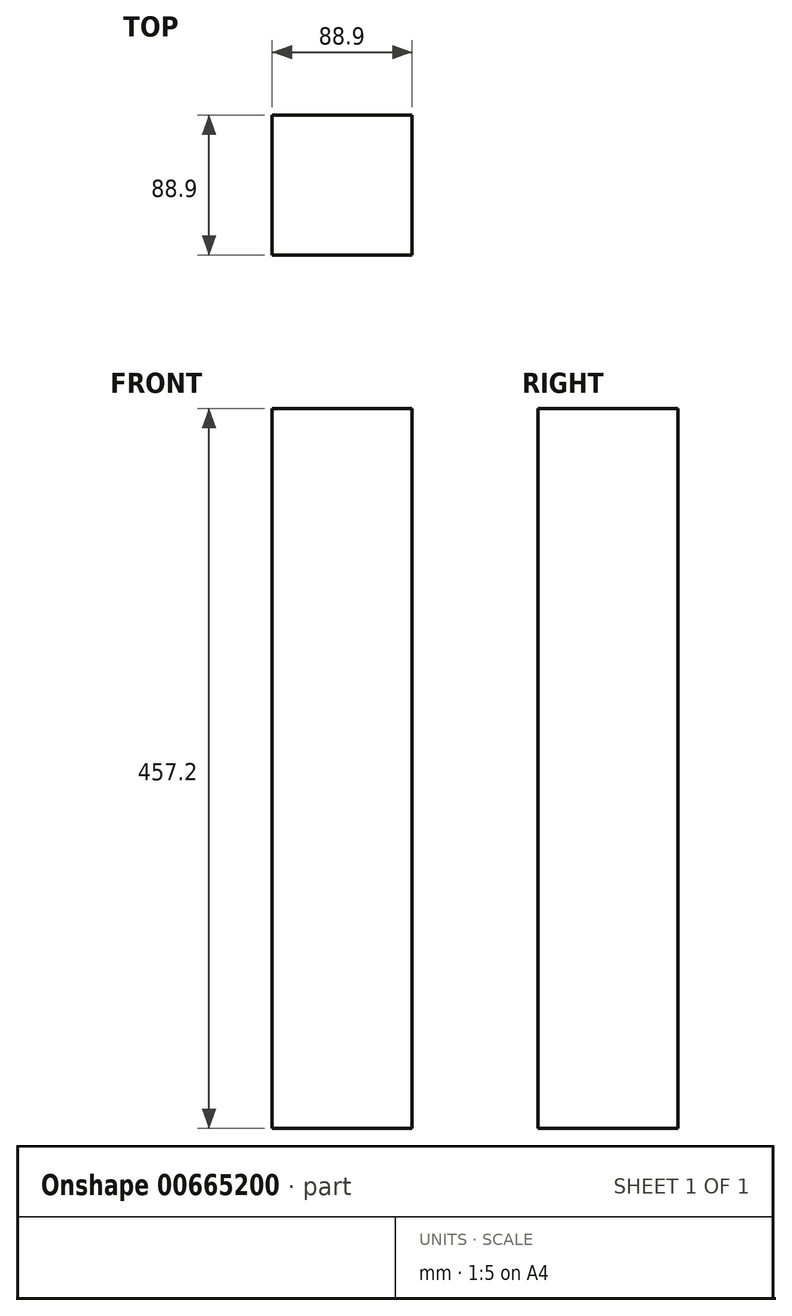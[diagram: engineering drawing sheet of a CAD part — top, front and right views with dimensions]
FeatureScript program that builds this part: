
annotation { "Feature Type Name" : "Feature", "Feature Type Description" : "" }
export const myFeature = defineFeature(function(context is Context, id is Id, definition is map)
    precondition{}
    {
        {
            var Q0;
            Q0=qCreatedBy(makeId("Top.planeOp"),FACE);
            var sketch = newSketch(context, id + "F0", { "sketchPlane" : qUnion([Q0])});
            skLineSegment(sketch, "E0.bottom", {"start": v(44.45, -44.45) * mm, "end": v(-44.45, -44.45) * mm});
            skLineSegment(sketch, "E0.top", {"start": v(44.45, 44.45) * mm, "end": v(-44.45, 44.45) * mm});
            skLineSegment(sketch, "E0.left", {"start": v(44.45, -44.45) * mm, "end": v(44.45, 44.45) * mm});
            skLineSegment(sketch, "E0.right", {"start": v(-44.45, -44.45) * mm, "end": v(-44.45, 44.45) * mm});
            skPoint(sketch, "E0.middle", {"position": v(0, 0) * mm});
            skSolve(sketch);
        }
        {
            var Q0;
            Q0=makeQuery(id+"F0.imprint","IMPRINT",FACE,{"disambiguationData":[TD([[makeQuery(id+"F0.imprint","IMPRINT",EDGE,{"derivedFrom":sQuery(id+"F0.wireOp",EDGE,"E0.bottom")}),-1.0]])]});
            extrude(context, id + "F1", {"entities" : qUnion([Q0]), "depth" : 457.2 * mm, "offsetDistance" : 25.4 * mm});
        }
    });
